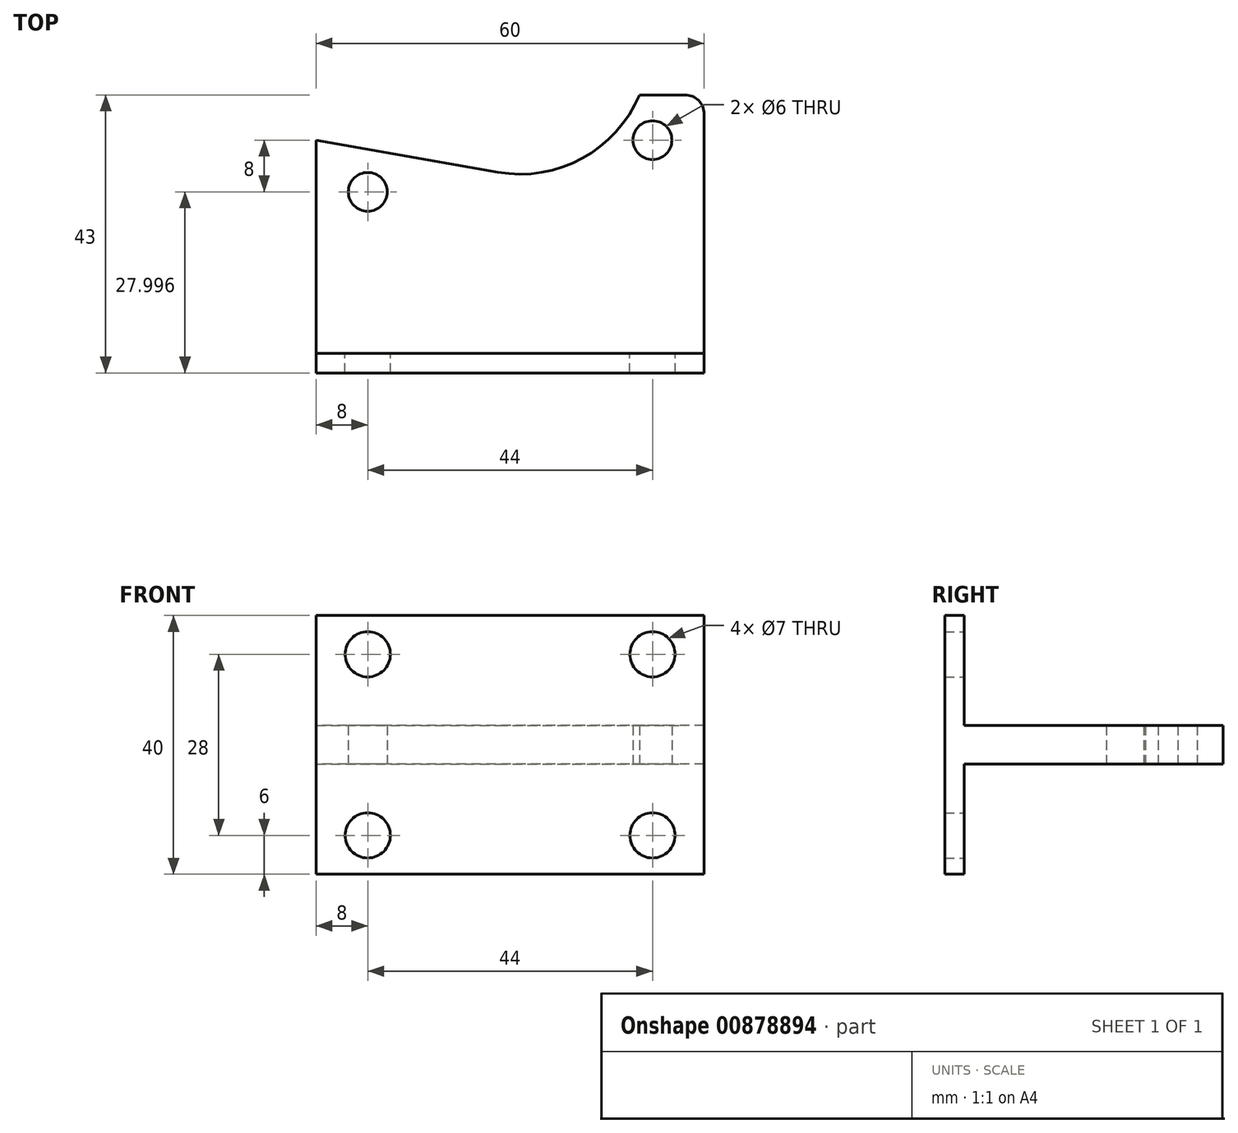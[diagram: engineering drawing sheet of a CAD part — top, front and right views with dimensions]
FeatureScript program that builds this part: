
annotation { "Feature Type Name" : "Feature", "Feature Type Description" : "" }
export const myFeature = defineFeature(function(context is Context, id is Id, definition is map)
    precondition{}
    {
        {
            var Q0;
            Q0=qCreatedBy(makeId("Top.planeOp"),FACE);
            var sketch = newSketch(context, id + "F0", { "sketchPlane" : qUnion([Q0])});
            skArc(sketch, "E0", {"start": v(-3.47, -19.7) * mm, "mid": v(9.58, -17.56) * mm, "end": v(18.44, -7.74) * mm});
            skLineSegment(sketch, "E1", {"start": v(18.44, -7.74) * mm, "end": v(25.44, -7.74) * mm});
            skLineSegment(sketch, "E2", {"start": v(28.44, -10.74) * mm, "end": v(28.44, -47.74) * mm});
            skLineSegment(sketch, "E3", {"start": v(28.44, -47.74) * mm, "end": v(-31.56, -47.74) * mm});
            skLineSegment(sketch, "E4", {"start": v(-31.56, -47.74) * mm, "end": v(-31.56, -14.74) * mm});
            skLineSegment(sketch, "E5", {"start": v(-31.56, -14.74) * mm, "end": v(-3.47, -19.7) * mm});
            skPoint(sketch, "E6.visualSharp", {"position": v(28.44, -7.74) * mm});
            skArc(sketch, "E6.filletArc", {"start": v(28.44, -10.74) * mm, "mid": v(27.56, -8.62) * mm, "end": v(25.44, -7.74) * mm});
            skCircle(sketch, "E7", {"center": v(-23.56, -22.74) * mm, "radius": 3 * mm});
            skCircle(sketch, "E8", {"center": v(20.44, -14.74) * mm, "radius": 3 * mm});
            skSolve(sketch);
        }
        {
            var Q0;
            Q0 = qSketchRegion(id + "F0", true);
            extrude(context, id + "F1", {"entities" : qUnion([Q0]), "endBound" : BoundingType.SYMMETRIC, "depth" : 6 * mm, "offsetDistance" : 25 * mm});
        }
        {
            var Q0;
            Q0=makeQuery(id+"F1.opExtrude","SWEPT_FACE",FACE,{"disambiguationData":[OSD([sQuery(id+"F0.wireOp",EDGE,"E3")])]});
            var sketch = newSketch(context, id + "F2", { "sketchPlane" : qUnion([Q0])});
            skLineSegment(sketch, "E9.bottom", {"start": v(-31.56, 20) * mm, "end": v(28.44, 20) * mm});
            skLineSegment(sketch, "E9.top", {"start": v(-31.56, -20) * mm, "end": v(28.44, -20) * mm});
            skLineSegment(sketch, "E9.left", {"start": v(-31.56, 20) * mm, "end": v(-31.56, -20) * mm});
            skLineSegment(sketch, "E9.right", {"start": v(28.44, 20) * mm, "end": v(28.44, -20) * mm});
            skCircle(sketch, "E10", {"center": v(-23.56, 14) * mm, "radius": 3.5 * mm});
            skCircle(sketch, "E11", {"center": v(-23.56, -14) * mm, "radius": 3.5 * mm});
            skCircle(sketch, "E12", {"center": v(20.44, -14) * mm, "radius": 3.5 * mm});
            skCircle(sketch, "E13", {"center": v(20.44, 14) * mm, "radius": 3.5 * mm});
            skSolve(sketch);
        }
        {
            var Q0;
            Q0 = qSketchRegion(id + "F2", true);
            extrude(context, id + "F3", {"entities" : qUnion([Q0]), "operationType" : NewBodyOperationType.ADD, "depth" : 3 * mm, "offsetDistance" : 25 * mm});
        }
    });
